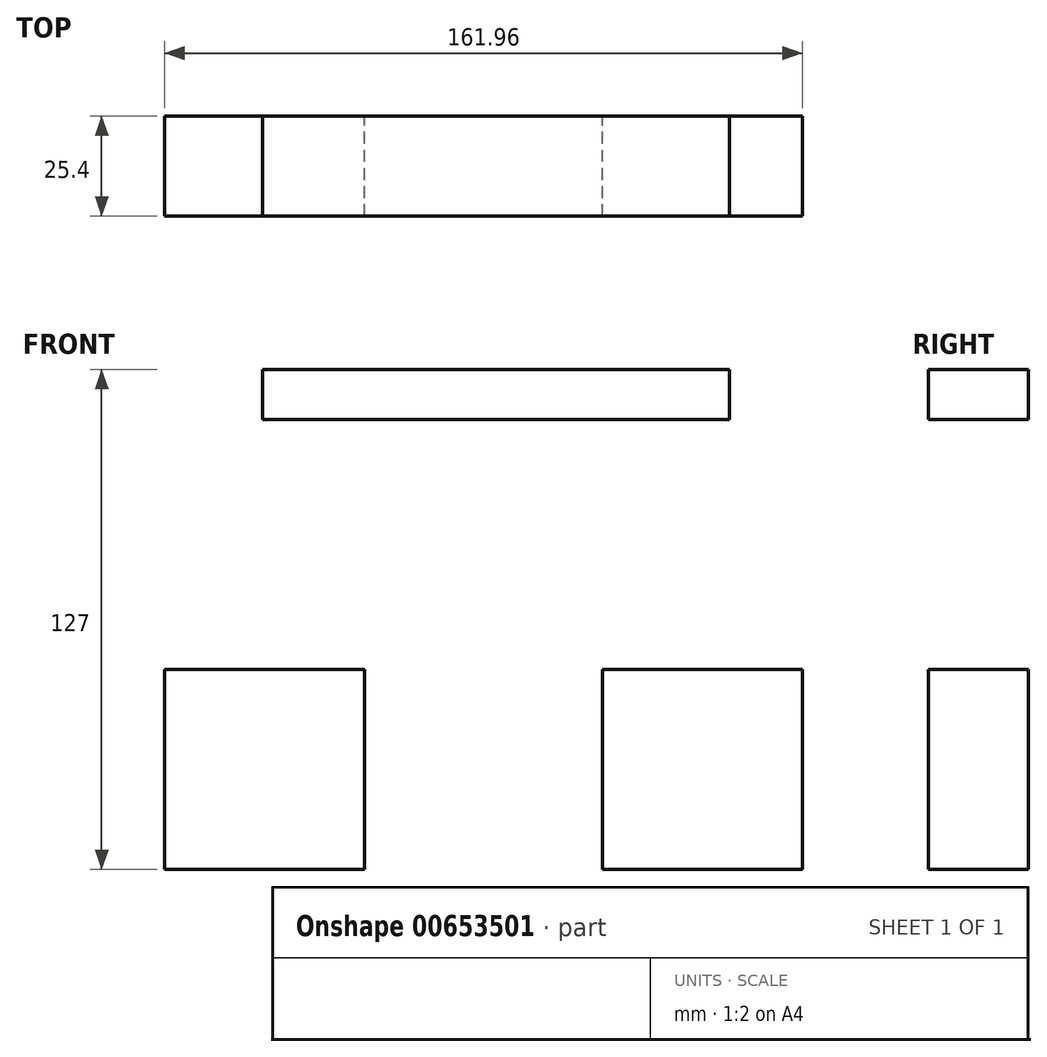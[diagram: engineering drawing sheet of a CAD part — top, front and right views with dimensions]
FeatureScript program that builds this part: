
annotation { "Feature Type Name" : "Feature", "Feature Type Description" : "" }
export const myFeature = defineFeature(function(context is Context, id is Id, definition is map)
    precondition{}
    {
        {
            var Q0;
            Q0=qCreatedBy(makeId("Front.planeOp"),FACE);
            var sketch = newSketch(context, id + "F0", { "sketchPlane" : qUnion([Q0])});
            skLineSegment(sketch, "E0.bottom", {"start": v(-88.22, -62.77) * mm, "end": v(-37.42, -62.77) * mm});
            skLineSegment(sketch, "E0.top", {"start": v(-88.22, -11.97) * mm, "end": v(-37.42, -11.97) * mm});
            skLineSegment(sketch, "E0.left", {"start": v(-88.22, -62.77) * mm, "end": v(-88.22, -11.97) * mm});
            skLineSegment(sketch, "E0.right", {"start": v(-37.42, -62.77) * mm, "end": v(-37.42, -11.97) * mm});
            skPoint(sketch, "E0.middle", {"position": v(-62.82, -37.37) * mm});
            skLineSegment(sketch, "E1.bottom", {"start": v(22.94, -62.77) * mm, "end": v(73.74, -62.77) * mm});
            skLineSegment(sketch, "E1.top", {"start": v(22.94, -11.97) * mm, "end": v(73.74, -11.97) * mm});
            skLineSegment(sketch, "E1.left", {"start": v(22.94, -62.77) * mm, "end": v(22.94, -11.97) * mm});
            skLineSegment(sketch, "E1.right", {"start": v(73.74, -62.77) * mm, "end": v(73.74, -11.97) * mm});
            skPoint(sketch, "E1.middle", {"position": v(48.34, -37.37) * mm});
            skLineSegment(sketch, "E2.bottom", {"start": v(-71.79, -11.97) * mm, "end": v(-63.42, -11.97) * mm});
            skLineSegment(sketch, "E2.top", {"start": v(-71.79, 64.23) * mm, "end": v(-63.42, 64.23) * mm});
            skLineSegment(sketch, "E2.left", {"start": v(-71.79, -11.97) * mm, "end": v(-71.79, 64.23) * mm});
            skLineSegment(sketch, "E2.right", {"start": v(-63.42, -11.97) * mm, "end": v(-63.42, 64.23) * mm});
            skLineSegment(sketch, "E3.bottom", {"start": v(-63.42, 64.23) * mm, "end": v(55.21, 64.23) * mm});
            skLineSegment(sketch, "E3.top", {"start": v(-63.42, 51.53) * mm, "end": v(55.21, 51.53) * mm});
            skLineSegment(sketch, "E3.left", {"start": v(-63.42, 64.23) * mm, "end": v(-63.42, 51.53) * mm});
            skLineSegment(sketch, "E3.right", {"start": v(55.21, 64.23) * mm, "end": v(55.21, 51.53) * mm});
            skLineSegment(sketch, "E4.bottom", {"start": v(55.21, 51.53) * mm, "end": v(48.34, 51.53) * mm});
            skLineSegment(sketch, "E4.top", {"start": v(55.21, -11.97) * mm, "end": v(48.34, -11.97) * mm});
            skLineSegment(sketch, "E4.left", {"start": v(55.21, 51.53) * mm, "end": v(55.21, -11.97) * mm});
            skLineSegment(sketch, "E4.right", {"start": v(48.34, 51.53) * mm, "end": v(48.34, -11.97) * mm});
            skSolve(sketch);
        }
        {
            var Q0;
            Q0=makeQuery(id+"F0.imprint","IMPRINT",FACE,{"disambiguationData":[TD([[makeQuery(id+"F0.imprint","IMPRINT",EDGE,{"derivedFrom":sQuery(id+"F0.wireOp",EDGE,"E1.bottom")}),1.0]])]});
            var Q1;
            Q1=makeQuery(id+"F0.imprint","IMPRINT",FACE,{"disambiguationData":[TD([[makeQuery(id+"F0.imprint","IMPRINT",EDGE,{"derivedFrom":sQuery(id+"F0.wireOp",EDGE,"E0.bottom")}),1.0]])]});
            var Q2;
            Q2=makeQuery(id+"F0.imprint","IMPRINT",FACE,{"disambiguationData":[TD([[makeQuery(id+"F0.imprint","IMPRINT",EDGE,{"derivedFrom":sQuery(id+"F0.wireOp",EDGE,"E2.bottom")}),1.0]])]});
            var Q3;
            Q3=makeQuery(id+"F0.imprint","IMPRINT",FACE,{"disambiguationData":[TD([[makeQuery(id+"F0.imprint","IMPRINT",EDGE,{"derivedFrom":sQuery(id+"F0.wireOp",EDGE,"E3.bottom")}),-1.0]])]});
            var Q4;
            Q4=makeQuery(id+"F0.imprint","IMPRINT",FACE,{"disambiguationData":[TD([[makeQuery(id+"F0.imprint","IMPRINT",EDGE,{"derivedFrom":sQuery(id+"F0.wireOp",EDGE,"E4.bottom")}),1.0]])]});
            extrude(context, id + "F1", {"entities" : qUnion([Q0, Q1, Q2, Q3, Q4]), "endBound" : BoundingType.SYMMETRIC, "depth" : 25.4 * mm, "offsetDistance" : 25.4 * mm});
        }
    });
